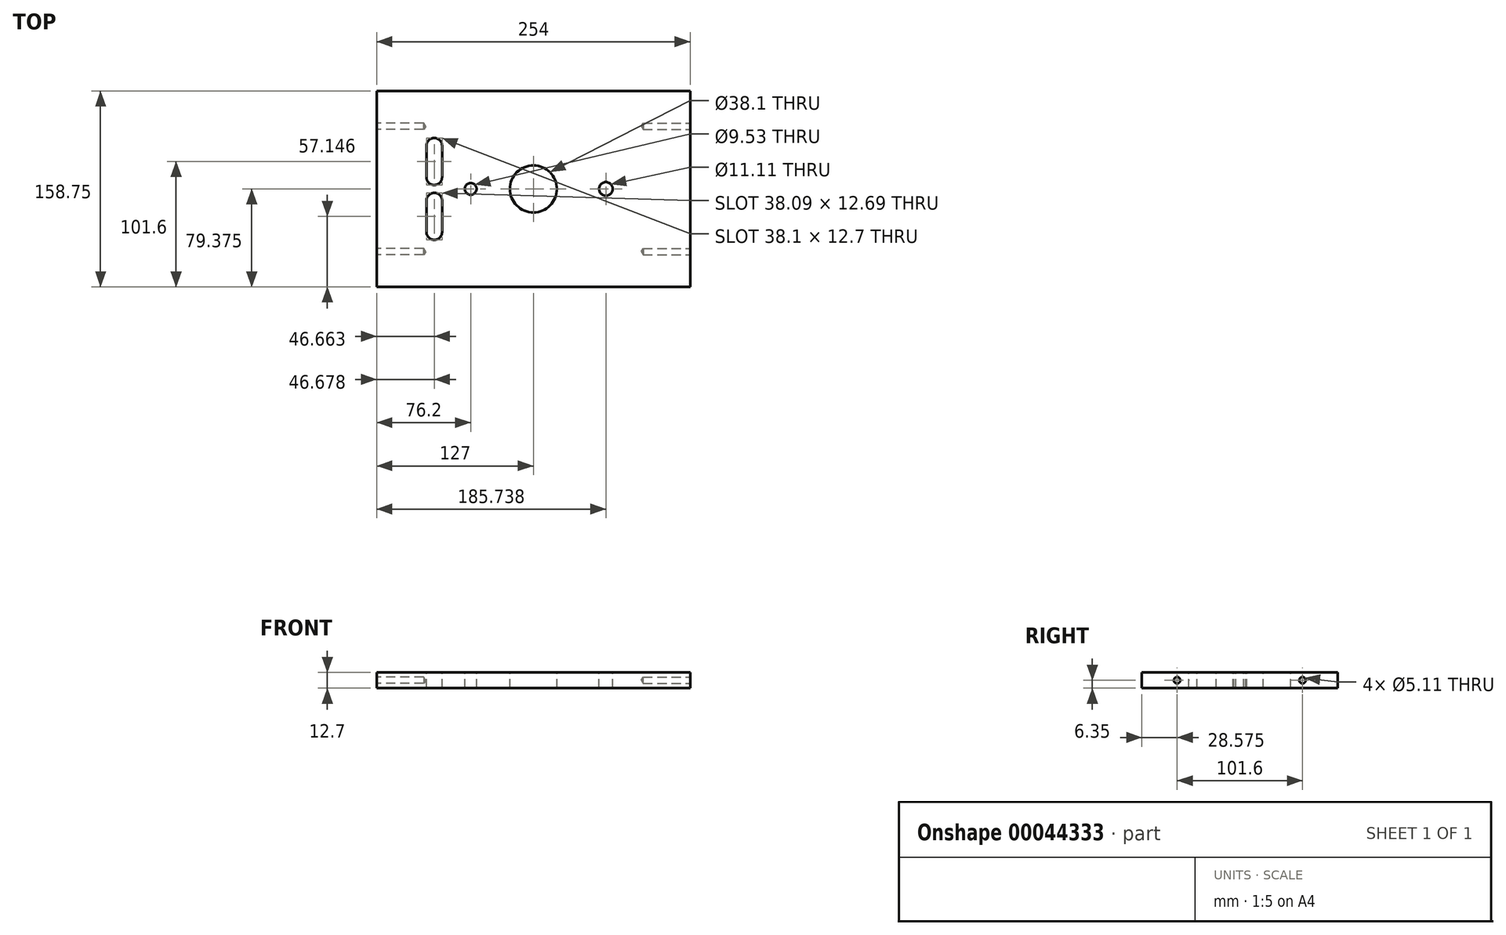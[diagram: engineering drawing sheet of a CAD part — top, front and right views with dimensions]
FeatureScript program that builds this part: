
annotation { "Feature Type Name" : "Feature", "Feature Type Description" : "" }
export const myFeature = defineFeature(function(context is Context, id is Id, definition is map)
    precondition{}
    {
        {
            var Q0;
            Q0=qCreatedBy(makeId("Top.planeOp"),FACE);
            var sketch = newSketch(context, id + "F0", { "sketchPlane" : qUnion([Q0])});
            skLineSegment(sketch, "E0", {"start": v(0, 0) * mm, "end": v(254, 0) * mm});
            skLineSegment(sketch, "E1", {"start": v(254, 0) * mm, "end": v(254, -158.75) * mm});
            skLineSegment(sketch, "E2", {"start": v(254, -158.75) * mm, "end": v(0, -158.75) * mm});
            skLineSegment(sketch, "E3", {"start": v(0, -158.75) * mm, "end": v(0, 0) * mm});
            skSolve(sketch);
        }
        {
            var Q0;
            Q0=makeQuery(id+"F0.imprint","IMPRINT",FACE,{"disambiguationData":[TD([[makeQuery(id+"F0.imprint","IMPRINT",EDGE,{"derivedFrom":sQuery(id+"F0.wireOp",EDGE,"E0")}),-1.0]])]});
            extrude(context, id + "F1", {"entities" : qUnion([Q0]), "depth" : 12.7 * mm});
        }
        {
            var Q0;
            Q0=makeQuery(id+"F1.opExtrude","CAP_FACE",FACE,{"disambiguationData":[OSD([sQuery(id+"F0.wireOp",EDGE,"E0"),sQuery(id+"F0.wireOp",EDGE,"E1"),sQuery(id+"F0.wireOp",EDGE,"E2"),sQuery(id+"F0.wireOp",EDGE,"E3")])],"isStart":false});
            var sketch = newSketch(context, id + "F2", { "sketchPlane" : qUnion([Q0])});
            skCircle(sketch, "E4", {"center": v(127, -79.38) * mm, "radius": 19.05 * mm});
            skSolve(sketch);
        }
        {
            var Q0;
            Q0=makeQuery(id+"F2.imprint","IMPRINT",FACE,{"disambiguationData":[TD([[makeQuery(id+"F2.imprint","IMPRINT",EDGE,{"derivedFrom":sQuery(id+"F2.wireOp",EDGE,"E4")}),1.0]])]});
            extrude(context, id + "F3", {"entities" : qUnion([Q0]), "operationType" : NewBodyOperationType.REMOVE, "endBound" : BoundingType.THROUGH_ALL, "oppositeDirection" : true, "depth" : 25.4 * mm});
        }
        {
            var Q0;
            Q0=makeQuery(id+"F1.opExtrude","SWEPT_FACE",FACE,{"disambiguationData":[OSD([sQuery(id+"F0.wireOp",EDGE,"E1")])]});
            var sketch = newSketch(context, id + "F4", { "sketchPlane" : qUnion([Q0])});
            skPoint(sketch, "E5", {"position": v(-28.58, 6.35) * mm});
            skPoint(sketch, "E6", {"position": v(-130.18, 6.35) * mm});
            skSolve(sketch);
        }
        {
            var Q0;
            Q0=sQuery(id+"F4.wireOp",VERTEX,"E5");
            var Q1;
            Q1=sQuery(id+"F4.wireOp",VERTEX,"E6");
            var Q2;
            Q2=makeQuery(id+"F1.opExtrude","SWEPT_BODY",BODY,{"disambiguationData":[OSD([sQuery(id+"F0.wireOp",EDGE,"E0"),sQuery(id+"F0.wireOp",EDGE,"E1"),sQuery(id+"F0.wireOp",EDGE,"E2"),sQuery(id+"F0.wireOp",EDGE,"E3")])]});
            hole(context, id + "F5", {"style" : HoleStyle.SIMPLE, "holeDiameter" : 5.1 * mm, "endStyle" : HoleEndStyle.BLIND, "holeDepth" : 38.1 * mm, "locations" : qUnion([Q0, Q1]), "scope" : qUnion([Q2])});
        }
        {
            var Q0;
            Q0=makeQuery(id+"F1.opExtrude","SWEPT_FACE",FACE,{"disambiguationData":[OSD([sQuery(id+"F0.wireOp",EDGE,"E3")])]});
            var sketch = newSketch(context, id + "F6", { "sketchPlane" : qUnion([Q0])});
            skPoint(sketch, "E7", {"position": v(28.58, 6.35) * mm});
            skPoint(sketch, "E8", {"position": v(130.18, 6.35) * mm});
            skSolve(sketch);
        }
        {
            var Q0;
            Q0=sQuery(id+"F6.wireOp",VERTEX,"E7");
            var Q1;
            Q1=sQuery(id+"F6.wireOp",VERTEX,"E8");
            var Q2;
            Q2=makeQuery(id+"F1.opExtrude","SWEPT_BODY",BODY,{"disambiguationData":[OSD([sQuery(id+"F0.wireOp",EDGE,"E0"),sQuery(id+"F0.wireOp",EDGE,"E1"),sQuery(id+"F0.wireOp",EDGE,"E2"),sQuery(id+"F0.wireOp",EDGE,"E3")])]});
            hole(context, id + "F7", {"style" : HoleStyle.SIMPLE, "holeDiameter" : 5.1 * mm, "endStyle" : HoleEndStyle.BLIND, "holeDepth" : 38.1 * mm, "locations" : qUnion([Q0, Q1]), "scope" : qUnion([Q2])});
        }
        {
            var Q0;
            Q0=makeQuery(id+"F1.opExtrude","CAP_FACE",FACE,{"disambiguationData":[OSD([sQuery(id+"F0.wireOp",EDGE,"E0"),sQuery(id+"F0.wireOp",EDGE,"E1"),sQuery(id+"F0.wireOp",EDGE,"E2"),sQuery(id+"F0.wireOp",EDGE,"E3")])],"isStart":false});
            var sketch = newSketch(context, id + "F8", { "sketchPlane" : qUnion([Q0])});
            skPoint(sketch, "E9", {"position": v(76.2, -79.38) * mm});
            skPoint(sketch, "E9.positionSnap0", {"position": v(0, -79.38) * mm});
            skLineSegment(sketch, "E10", {"start": v(127, 0) * mm, "end": v(127, -158.75) * mm});
            skSolve(sketch);
        }
        {
            var Q0;
            Q0=sQuery(id+"F8.wireOp",VERTEX,"E9");
            var Q1;
            Q1=makeQuery(id+"F1.opExtrude","SWEPT_BODY",BODY,{"disambiguationData":[OSD([sQuery(id+"F0.wireOp",EDGE,"E0"),sQuery(id+"F0.wireOp",EDGE,"E1"),sQuery(id+"F0.wireOp",EDGE,"E2"),sQuery(id+"F0.wireOp",EDGE,"E3")])]});
            hole(context, id + "F9", {"style" : HoleStyle.SIMPLE, "holeDiameter" : 9.52 * mm, "endStyle" : HoleEndStyle.THROUGH, "locations" : qUnion([Q0]), "scope" : qUnion([Q1])});
        }
        {
            var Q0;
            Q0=makeQuery(id+"F1.opExtrude","CAP_FACE",FACE,{"disambiguationData":[OSD([sQuery(id+"F0.wireOp",EDGE,"E0"),sQuery(id+"F0.wireOp",EDGE,"E1"),sQuery(id+"F0.wireOp",EDGE,"E2"),sQuery(id+"F0.wireOp",EDGE,"E3")])],"isStart":false});
            var sketch = newSketch(context, id + "F10", { "sketchPlane" : qUnion([Q0])});
            skPoint(sketch, "E11", {"position": v(185.74, -79.38) * mm});
            skPoint(sketch, "E11.positionSnap0", {"position": v(0, -79.38) * mm});
            skLineSegment(sketch, "E12", {"start": v(127, -54.88) * mm, "end": v(127, -117.6) * mm});
            skPoint(sketch, "E12.startSnap0", {"position": v(127, 0) * mm});
            skSolve(sketch);
        }
        {
            var Q0;
            Q0=sQuery(id+"F10.wireOp",VERTEX,"E11");
            var Q1;
            Q1=makeQuery(id+"F1.opExtrude","SWEPT_BODY",BODY,{"disambiguationData":[OSD([sQuery(id+"F0.wireOp",EDGE,"E0"),sQuery(id+"F0.wireOp",EDGE,"E1"),sQuery(id+"F0.wireOp",EDGE,"E2"),sQuery(id+"F0.wireOp",EDGE,"E3")])]});
            hole(context, id + "F11", {"style" : HoleStyle.SIMPLE, "holeDiameter" : 11.1 * mm, "endStyle" : HoleEndStyle.THROUGH, "locations" : qUnion([Q0]), "scope" : qUnion([Q1])});
        }
        {
            var Q0;
            Q0=makeQuery(id+"F1.opExtrude","CAP_FACE",FACE,{"disambiguationData":[OSD([sQuery(id+"F0.wireOp",EDGE,"E0"),sQuery(id+"F0.wireOp",EDGE,"E1"),sQuery(id+"F0.wireOp",EDGE,"E2"),sQuery(id+"F0.wireOp",EDGE,"E3")])],"isStart":false});
            var sketch = newSketch(context, id + "F12", { "sketchPlane" : qUnion([Q0])});
            skPoint(sketch, "E13", {"position": v(46.66, -69.85) * mm});
            skLineSegment(sketch, "E14", {"start": v(76.2, -74.61) * mm, "end": v(76.2, -84.14) * mm});
            skLineSegment(sketch, "E15", {"start": v(80.96, -79.38) * mm, "end": v(71.44, -79.38) * mm});
            skArc(sketch, "E16", {"start": v(40.31, -69.85) * mm, "mid": v(46.67, -76.2) * mm, "end": v(53.01, -69.83) * mm});
            skArc(sketch, "E17", {"start": v(53.01, -44.47) * mm, "mid": v(46.65, -38.1) * mm, "end": v(40.31, -44.49) * mm});
            skLineSegment(sketch, "E18", {"start": v(53.01, -44.47) * mm, "end": v(53.01, -69.87) * mm});
            skLineSegment(sketch, "E19", {"start": v(40.31, -44.49) * mm, "end": v(40.31, -69.85) * mm});
            skSolve(sketch);
        }
        {
            var Q0;
            Q0 = qSketchRegion(id + "F12", true);
            var Q1;
            Q1=makeQuery(id+"F1.opExtrude","CAP_FACE",FACE,{"disambiguationData":[OSD([sQuery(id+"F0.wireOp",EDGE,"E0"),sQuery(id+"F0.wireOp",EDGE,"E1"),sQuery(id+"F0.wireOp",EDGE,"E2"),sQuery(id+"F0.wireOp",EDGE,"E3")])],"isStart":false});
            extrude(context, id + "F13", {"entities" : qUnion([Q0]), "operationType" : NewBodyOperationType.REMOVE, "endBound" : BoundingType.THROUGH_ALL, "oppositeDirection" : true, "endBoundEntityFace" : qUnion([Q1]), "depth" : 25.4 * mm});
        }
        {
            var Q0;
            Q0=makeQuery(id+"F1.opExtrude","CAP_FACE",FACE,{"disambiguationData":[OSD([sQuery(id+"F0.wireOp",EDGE,"E0"),sQuery(id+"F0.wireOp",EDGE,"E1"),sQuery(id+"F0.wireOp",EDGE,"E2"),sQuery(id+"F0.wireOp",EDGE,"E3")])],"isStart":false});
            var sketch = newSketch(context, id + "F14", { "sketchPlane" : qUnion([Q0])});
            skPoint(sketch, "E20", {"position": v(46.67, -88.9) * mm});
            skPoint(sketch, "E20.positionSnap0", {"position": v(46.67, -76.2) * mm});
            skArc(sketch, "E21", {"start": v(53.01, -88.94) * mm, "mid": v(46.7, -82.56) * mm, "end": v(40.33, -88.9) * mm});
            skArc(sketch, "E22", {"start": v(40.33, -113.94) * mm, "mid": v(46.5, -120.65) * mm, "end": v(53.02, -114.3) * mm});
            skLineSegment(sketch, "E23", {"start": v(40.33, -88.9) * mm, "end": v(40.33, -114.66) * mm});
            skLineSegment(sketch, "E24", {"start": v(53.01, -88.94) * mm, "end": v(53.02, -114.3) * mm});
            skSolve(sketch);
        }
        {
            var Q0;
            Q0 = qSketchRegion(id + "F14", true);
            extrude(context, id + "F15", {"entities" : qUnion([Q0]), "operationType" : NewBodyOperationType.REMOVE, "endBound" : BoundingType.THROUGH_ALL, "oppositeDirection" : true, "depth" : 25.4 * mm});
        }
    });
